# Revit family: DSP_A3-Kal-Aluminium-900x2125
name_source: partatom
category: Doors
revit_build: Autodesk Revit 2016 (Build: 20150220_1215(x64)
units: mm (PartAtom-declared; Revit-internal decimal feet)

## family parameters
Always vertical = Yes
Cut with Voids When Loaded = No
Host = Wall
Room Calculation Point = No
Shared = No

## types (3) — shared parameters
Frame Size = 110 mm  [stored 0.360892 ft]
Frame Width = 44 mm
Function = Interior
Inset = 110 mm  [stored 0.360892 ft]
Material Door = HORIZONTAL SLATTED
Material Frame = Default TIMBER FRAME
PANEL MATERIAL = <By Category>
Panel Width = 40 mm  [stored 0.131234 ft]
Wall Closure = By host

## per-type parameters (varying)
| type | Description | Height | Rough Height | Rough Width | Width |
| EXT DOOR | STANDARD ALUMINIUM DOOR WITH SAFETY GLASS | 2125 mm | 2032 mm | 813 mm | 900 mm  [stored 2.95276 ft] |
| EXT DOOR 680X2465 | STANDARD ALUMINIUM DOOR WITH SAFETY GLASS | 2465 mm  [stored 8.08727 ft] | 2372 mm | 593 mm  [stored 1.94554 ft] | 680 mm  [stored 2.23097 ft] |
| EXT DOOR 2 | 813x2032 INTERNAL DOOR TO DEVELOPERS SPEC. | 2125 mm | 2032 mm | 813 mm | 900 mm  [stored 2.95276 ft] |

note: [stored X ft] marks values corroborated as IEEE doubles in the binary element streams (Revit-internal decimal feet)

## geometry (parser evidence)
native form markers: Sweep x3
no freeform markers — native parametric forms only
